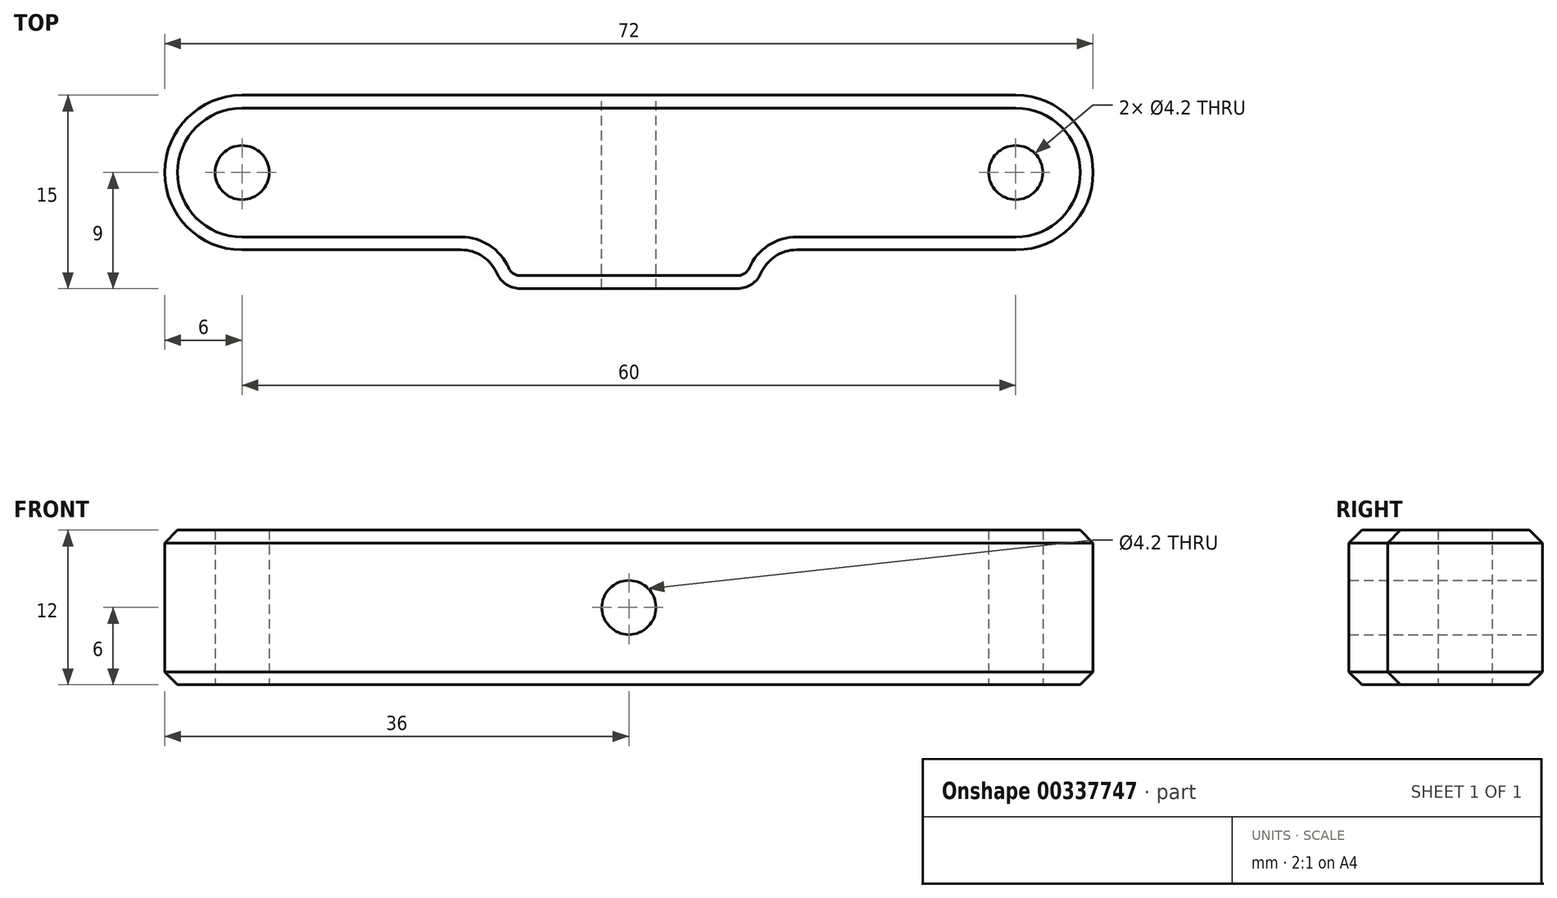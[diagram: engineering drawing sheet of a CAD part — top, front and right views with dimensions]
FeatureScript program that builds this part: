
annotation { "Feature Type Name" : "Feature", "Feature Type Description" : "" }
export const myFeature = defineFeature(function(context is Context, id is Id, definition is map)
    precondition{}
    {
        {
            var Q0;
            Q0=qCreatedBy(makeId("Top.planeOp"),FACE);
            var sketch = newSketch(context, id + "F0", { "sketchPlane" : qUnion([Q0])});
            skLineSegment(sketch, "E0.bottom", {"start": v(8.42, -9) * mm, "end": v(-8.42, -9) * mm});
            skLineSegment(sketch, "E0.left", {"start": v(10, -9) * mm, "end": v(10, -9) * mm});
            skLineSegment(sketch, "E0.right", {"start": v(-10, -9) * mm, "end": v(-10, -9) * mm});
            skPoint(sketch, "E0.middle", {"position": v(0, 0) * mm});
            skCircle(sketch, "E1", {"center": v(-30, 0) * mm, "radius": 2.1 * mm});
            skCircle(sketch, "E2", {"center": v(30, 0) * mm, "radius": 2.1 * mm});
            skLineSegment(sketch, "E3", {"start": v(-30, 0) * mm, "end": v(30, 0) * mm, "construction": true});
            skArc(sketch, "E4.0.startCap", {"start": v(-30, -6) * mm, "mid": v(-36, 0) * mm, "end": v(-30, 6) * mm});
            skArc(sketch, "E4.0.endCap", {"start": v(30, 6) * mm, "mid": v(36, 0) * mm, "end": v(30, -6) * mm});
            skLineSegment(sketch, "E4.0.left", {"start": v(-30, 6) * mm, "end": v(30, 6) * mm});
            skLineSegment(sketch, "E4.0.right", {"start": v(-30, -6) * mm, "end": v(-13, -6) * mm});
            skLineSegment(sketch, "E5.trimOffspring", {"start": v(13, -6) * mm, "end": v(30, -6) * mm});
            skPoint(sketch, "E6.orphan", {"position": v(-10, 9) * mm});
            skPoint(sketch, "E7.trimOffspring.end.orphan", {"position": v(10, 9) * mm});
            skPoint(sketch, "E8.visualSharp", {"position": v(-10, -6) * mm});
            skArc(sketch, "E8.filletArc", {"start": v(-10.25, -7.8) * mm, "mid": v(-11.36, -6.5) * mm, "end": v(-13, -6) * mm});
            skPoint(sketch, "E9.visualSharp", {"position": v(10, -6) * mm});
            skArc(sketch, "E9.filletArc", {"start": v(13, -6) * mm, "mid": v(11.36, -6.5) * mm, "end": v(10.25, -7.8) * mm});
            skPoint(sketch, "E10.visualSharp", {"position": v(-10, -9) * mm});
            skArc(sketch, "E10.filletArc", {"start": v(-10.25, -7.8) * mm, "mid": v(-9.51, -8.67) * mm, "end": v(-8.42, -9) * mm});
            skPoint(sketch, "E11.visualSharp", {"position": v(10, -9) * mm});
            skArc(sketch, "E11.filletArc", {"start": v(8.42, -9) * mm, "mid": v(9.51, -8.67) * mm, "end": v(10.25, -7.8) * mm});
            skSolve(sketch);
        }
        {
            var Q0;
            Q0=makeQuery(id+"F0.imprint","IMPRINT",FACE,{"disambiguationData":[TD([[makeQuery(id+"F0.imprint","IMPRINT",EDGE,{"derivedFrom":sQuery(id+"F0.wireOp",EDGE,"E0.bottom")}),-1.0]])]});
            extrude(context, id + "F1", {"entities" : qUnion([Q0]), "depth" : 12 * mm, "offsetDistance" : 25 * mm});
        }
        {
            var Q0;
            Q0=makeQuery(id+"F1.opExtrude","SWEPT_FACE",FACE,{"disambiguationData":[OSD([sQuery(id+"F0.wireOp",EDGE,"E4.0.left")])]});
            var sketch = newSketch(context, id + "F2", { "sketchPlane" : qUnion([Q0])});
            skLineSegment(sketch, "E12", {"start": v(0, 12) * mm, "end": v(0, 0) * mm, "construction": true});
            skCircle(sketch, "E13", {"center": v(0, 6) * mm, "radius": 2.1 * mm});
            skSolve(sketch);
        }
        {
            var Q0;
            Q0=makeQuery(id+"F2.imprint","IMPRINT",FACE,{"disambiguationData":[TD([[makeQuery(id+"F2.imprint","IMPRINT",EDGE,{"derivedFrom":sQuery(id+"F2.wireOp",EDGE,"E13")}),1.0]])]});
            extrude(context, id + "F3", {"entities" : qUnion([Q0]), "operationType" : NewBodyOperationType.REMOVE, "endBound" : BoundingType.THROUGH_ALL, "oppositeDirection" : true, "depth" : 25 * mm, "offsetDistance" : 25 * mm});
        }
        {
            var Q0;
            Q0=makeQuery(id+"F1.opExtrude","CAP_EDGE",EDGE,{"disambiguationData":[OSD([sQuery(id+"F0.wireOp",EDGE,"E0.bottom")])],"isStart":false});
            var Q1;
            Q1=makeQuery(id+"F1.opExtrude","CAP_EDGE",EDGE,{"disambiguationData":[OSD([sQuery(id+"F0.wireOp",EDGE,"E4.0.left")])],"isStart":true});
            chamfer(context, id + "F4", {"entities" : qUnion([Q0, Q1]), "width" : 1 * mm, "tangentPropagation" : true});
        }
    });
